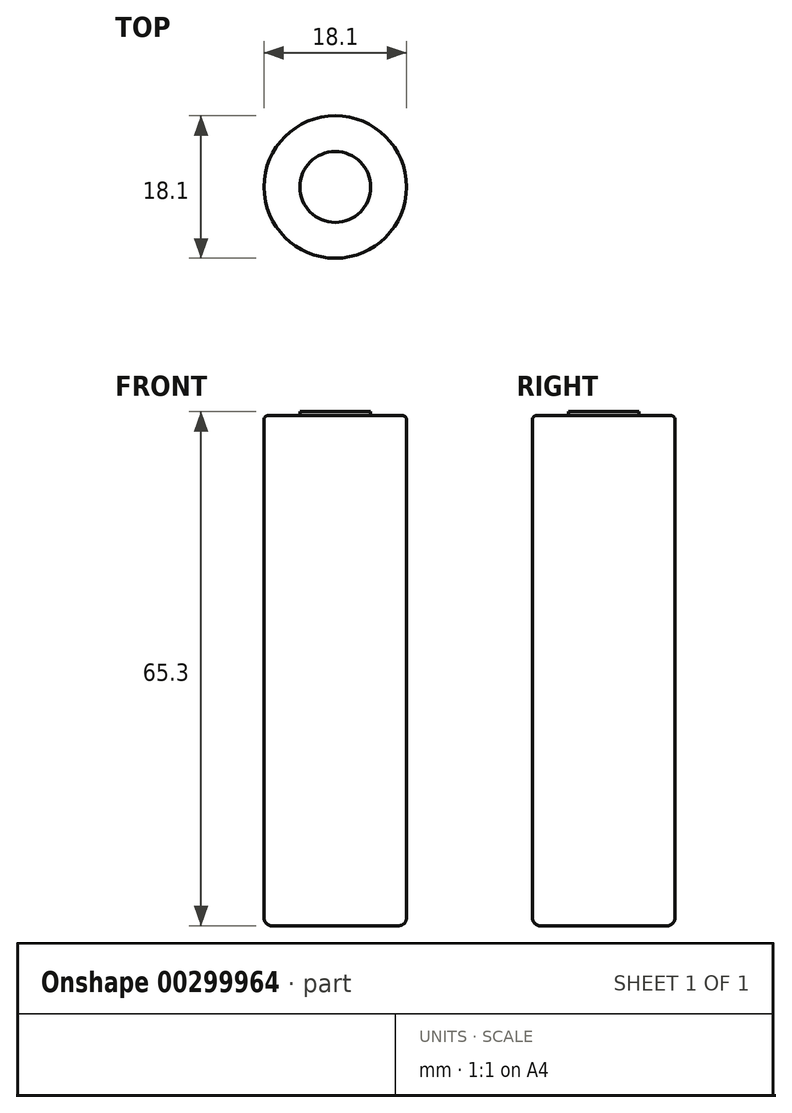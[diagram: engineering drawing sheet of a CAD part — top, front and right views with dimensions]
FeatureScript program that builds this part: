
annotation { "Feature Type Name" : "Feature", "Feature Type Description" : "" }
export const myFeature = defineFeature(function(context is Context, id is Id, definition is map)
    precondition{}
    {
        {
            var Q0;
            Q0=qCreatedBy(makeId("Top.planeOp"),FACE);
            var sketch = newSketch(context, id + "F0", { "sketchPlane" : qUnion([Q0])});
            skCircle(sketch, "E0", {"center": v(0, 0) * mm, "radius": 9.05 * mm});
            skSolve(sketch);
        }
        {
            var Q0;
            Q0=makeQuery(id+"F0.imprint","IMPRINT",FACE,{"disambiguationData":[TD([[makeQuery(id+"F0.imprint","IMPRINT",EDGE,{"derivedFrom":sQuery(id+"F0.wireOp",EDGE,"E0")}),1.0]])]});
            extrude(context, id + "F1", {"entities" : qUnion([Q0]), "depth" : 64.8 * mm});
        }
        {
            var Q0;
            Q0=makeQuery(id+"F1.opExtrude","CAP_EDGE",EDGE,{"disambiguationData":[OSD([sQuery(id+"F0.wireOp",EDGE,"E0")])],"isStart":true});
            fillet(context, id + "F2", {"entities" : qUnion([Q0]), "radius" : 1 * mm, "tangentPropagation" : true, "allowEdgeOverflow" : false});
        }
        {
            var Q0;
            Q0=makeQuery(id+"F1.opExtrude","CAP_FACE",FACE,{"disambiguationData":[OSD([sQuery(id+"F0.wireOp",EDGE,"E0")])],"isStart":false});
            var sketch = newSketch(context, id + "F3", { "sketchPlane" : qUnion([Q0])});
            skCircle(sketch, "E1", {"center": v(0, 0) * mm, "radius": 4.5 * mm});
            skSolve(sketch);
        }
        {
            var Q0;
            Q0=makeQuery(id+"F3.imprint","IMPRINT",FACE,{"disambiguationData":[TD([[makeQuery(id+"F3.imprint","IMPRINT",EDGE,{"derivedFrom":sQuery(id+"F3.wireOp",EDGE,"E1")}),1.0]])]});
            extrude(context, id + "F4", {"entities" : qUnion([Q0]), "operationType" : NewBodyOperationType.ADD, "depth" : 0.5 * mm});
        }
        {
            var Q0;
            Q0=makeQuery(id+"F1.opExtrude","CAP_EDGE",EDGE,{"disambiguationData":[OSD([sQuery(id+"F0.wireOp",EDGE,"E0")])],"isStart":false});
            fillet(context, id + "F5", {"entities" : qUnion([Q0]), "radius" : 0.5 * mm, "tangentPropagation" : true, "allowEdgeOverflow" : false});
        }
    });
